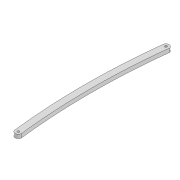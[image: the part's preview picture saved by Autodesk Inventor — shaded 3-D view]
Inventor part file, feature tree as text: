
AUTODESK INVENTOR PART (.ipt)
format: ipt  version: 2022 (Build 260153000, 153)  size: 94,720 bytes
history: native  units: mm
features: extrude x1, sketch x1
ambient origin geometry x8: Origin, YZ Plane, XZ Plane, XY Plane, X Axis, Y Axis, Z Axis, Center Point
bodies: Solid1 (feature_tree)
feature tree (2):
  extrude  "Extrusion1"  Depth=1000.0mm
  sketch  "Sketch1"  dims[d0=3.3mm d1=3.3mm d2=10.0mm d3=230.652mm d6=6.0mm d7=0.0mm d14=1000.0mm d15=1000.0mm]
